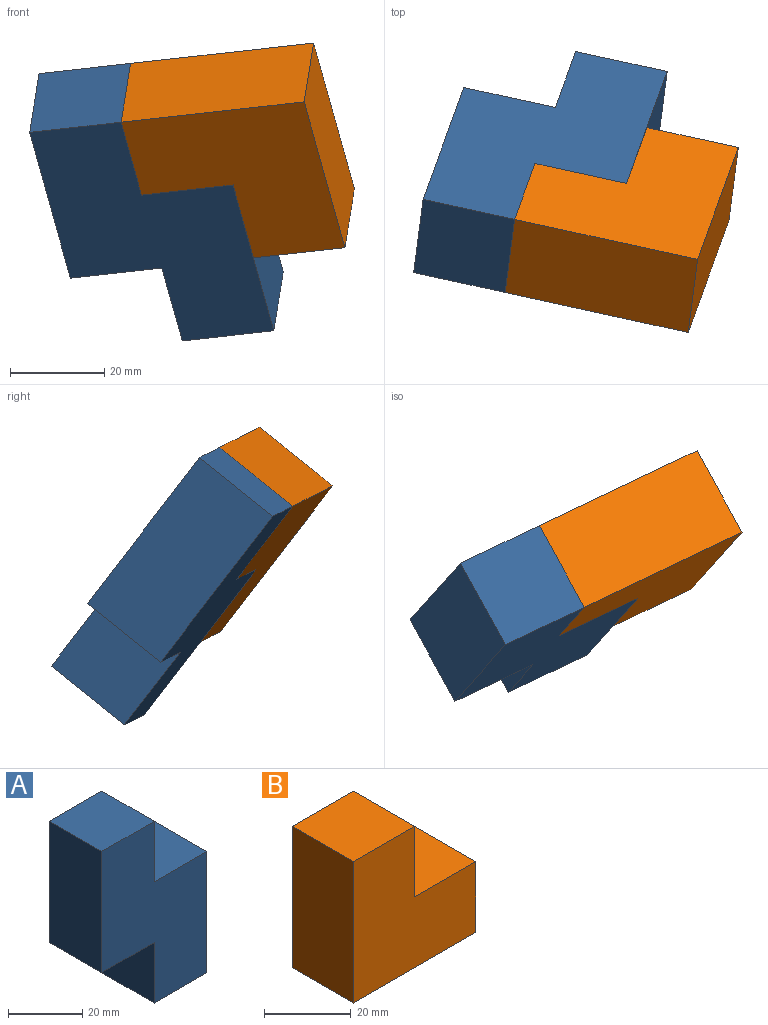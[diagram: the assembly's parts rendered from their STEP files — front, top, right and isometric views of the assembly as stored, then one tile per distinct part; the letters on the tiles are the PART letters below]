
ASSEMBLY  parts=2 mates=1
PART A: 10 faces, bbox 40x20x60 mm
  f0: plane 20x20mm, normal (0,0,1), area 400mm2, adj f1,f7,f8,f9
  f1: plane 40x20mm, normal (-1,0,0), area 800mm2, adj f0,f2,f8,f9
  f2: plane 20x20mm, normal (0,0,-1), area 400mm2, adj f1,f3,f8,f9
  f3: plane 20x20mm, normal (-1,0,0), area 400mm2, adj f2,f4,f8,f9
  f4: plane 20x20mm, normal (0,0,-1), area 400mm2, adj f3,f5,f8,f9
  f5: plane 40x20mm, normal (1,0,0), area 800mm2, adj f4,f6,f8,f9
  f6: plane 20x20mm, normal (0,0,1), area 400mm2, adj f5,f7,f8,f9
  f7: plane 20x20mm, normal (1,0,0), area 400mm2, adj f0,f6,f8,f9
  f8: plane 60x40mm, normal (0,-1,0), area 1600mm2, adj f0,f1,f2,f3,f4,f5,f6,f7
  f9: plane 60x40mm, normal (0,1,0), area 1600mm2, adj f0,f1,f2,f3,f4,f5,f6,f7
PART B: 8 faces, bbox 40x20x40 mm
  f0: plane 20x20mm, normal (0,0,1), area 400mm2, adj f1,f5,f6,f7
  f1: plane 40x20mm, normal (-1,0,0), area 800mm2, adj f0,f2,f6,f7
  f2: plane 40x20mm, normal (0,0,-1), area 800mm2, adj f1,f3,f6,f7
  f3: plane 20x20mm, normal (1,0,0), area 400mm2, adj f2,f4,f6,f7
  f4: plane 20x20mm, normal (0,0,1), area 400mm2, adj f3,f5,f6,f7
  f5: plane 20x20mm, normal (1,0,0), area 400mm2, adj f0,f4,f6,f7
  f6: plane 40x40mm, normal (0,-1,0), area 1200mm2, adj f0,f1,f2,f3,f4,f5
  f7: plane 40x40mm, normal (0,1,0), area 1200mm2, adj f0,f1,f2,f3,f4,f5
PLACE A rot(axis=(0.94,-0.25,-0.24),40.5deg) t=(-9.63,11.51,-1.23)mm
PLACE B rot(axis=(-0.76,-0.18,0.63),146.4deg) t=(13.83,-9.76,-10.61)mm
MATE fastened B.f0 <-> A.f7  axis (-0.97,0.21,-0.11) through (-35.86,-12.98,1.34)mm
